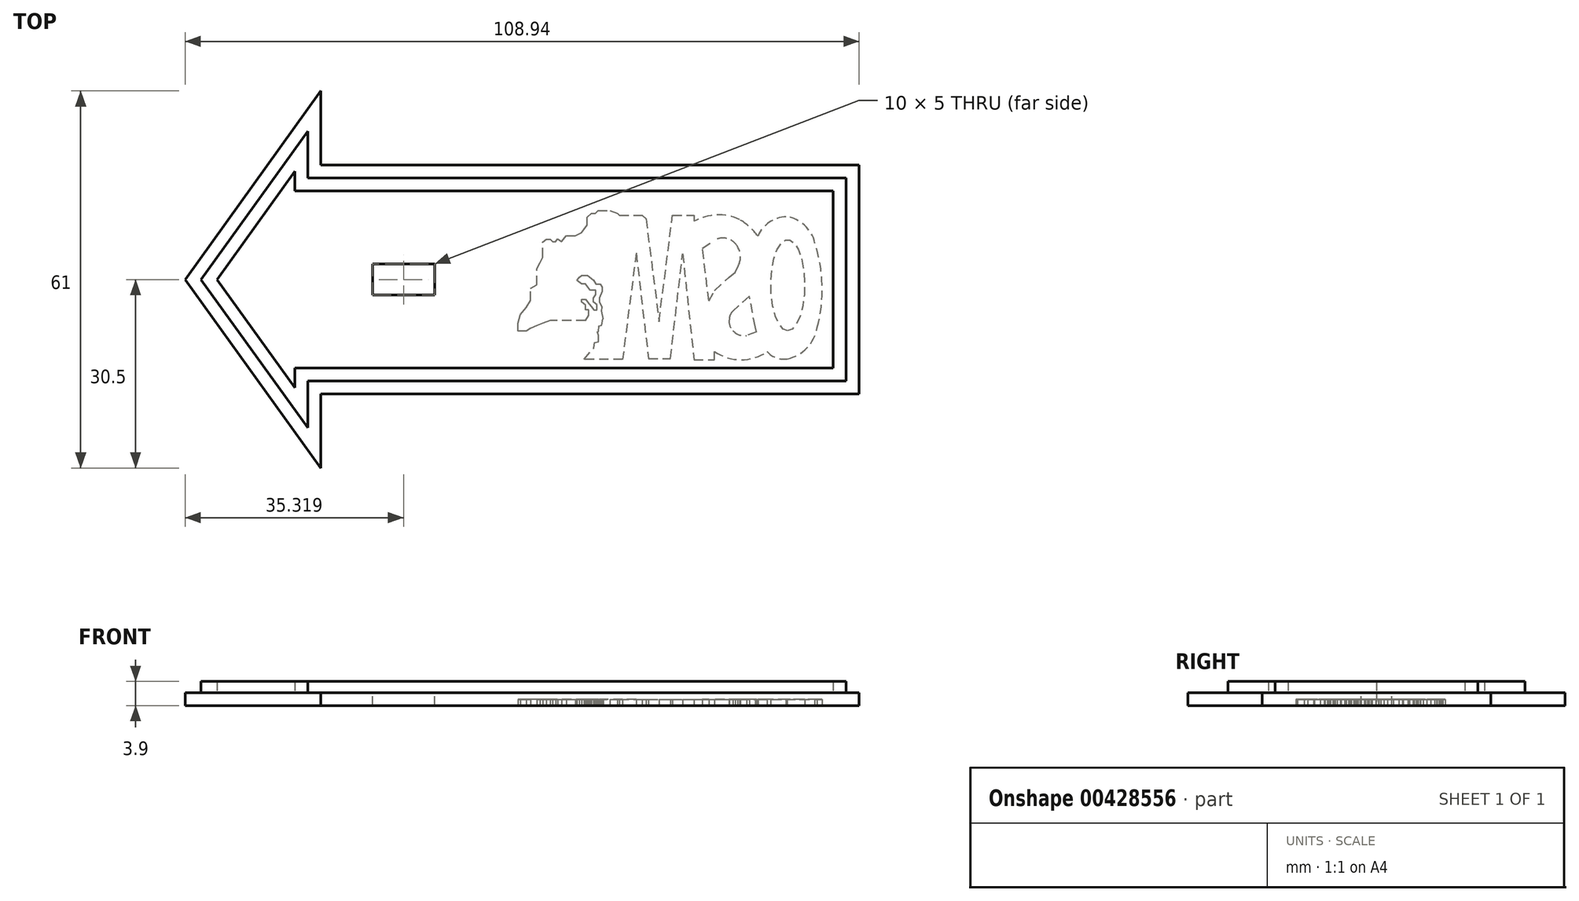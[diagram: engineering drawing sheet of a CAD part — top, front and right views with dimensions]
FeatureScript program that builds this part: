
annotation { "Feature Type Name" : "Feature", "Feature Type Description" : "" }
export const myFeature = defineFeature(function(context is Context, id is Id, definition is map)
    precondition{}
    {
        {
            var Q0;
            Q0=qCreatedBy(makeId("Top.planeOp"),FACE);
            var sketch = newSketch(context, id + "F0", { "sketchPlane" : qUnion([Q0])});
            skLineSegment(sketch, "E0.0", {"start": v(61.6, 18.5) * mm, "end": v(61.6, -18.5) * mm});
            skLineSegment(sketch, "E0.1", {"start": v(-25.4, 18.5) * mm, "end": v(61.6, 18.5) * mm});
            skLineSegment(sketch, "E0.3", {"start": v(-25.4, -18.5) * mm, "end": v(61.6, -18.5) * mm});
            skLineSegment(sketch, "E1", {"start": v(-25.4, 18.5) * mm, "end": v(-25.4, 30.5) * mm});
            skLineSegment(sketch, "E2", {"start": v(-25.4, 30.5) * mm, "end": v(-47.35, 0) * mm});
            skLineSegment(sketch, "E3", {"start": v(-47.35, 0) * mm, "end": v(-25.4, -30.5) * mm});
            skLineSegment(sketch, "E4", {"start": v(-25.4, -30.5) * mm, "end": v(-25.4, -18.5) * mm});
            skPoint(sketch, "E5", {"position": v(61.6, 0) * mm});
            skSolve(sketch);
        }
        {
            var Q0;
            Q0=makeQuery(id+"F0.imprint","IMPRINT",FACE,{"disambiguationData":[TD([[makeQuery(id+"F0.imprint","IMPRINT",EDGE,{"derivedFrom":sQuery(id+"F0.wireOp",EDGE,"E0.0")}),-1.0]])]});
            extrude(context, id + "F1", {"entities" : qUnion([Q0]), "depth" : 2.1 * mm});
        }
        {
            var Q0;
            Q0=makeQuery(id+"F1.opExtrude","CAP_FACE",FACE,{"disambiguationData":[OSD([sQuery(id+"F0.wireOp",EDGE,"E0.0"),sQuery(id+"F0.wireOp",EDGE,"E0.1"),sQuery(id+"F0.wireOp",EDGE,"E0.3"),sQuery(id+"F0.wireOp",EDGE,"E1"),sQuery(id+"F0.wireOp",EDGE,"E2"),sQuery(id+"F0.wireOp",EDGE,"E3"),sQuery(id+"F0.wireOp",EDGE,"E4")])],"isStart":false});
            var sketch = newSketch(context, id + "F2", { "sketchPlane" : qUnion([Q0])});
            skLineSegment(sketch, "E6.0", {"start": v(61.6, 18.5) * mm, "end": v(61.6, -18.5) * mm, "construction": true});
            skLineSegment(sketch, "E6.1", {"start": v(-25.4, 18.5) * mm, "end": v(61.6, 18.5) * mm, "construction": true});
            skLineSegment(sketch, "E6.3", {"start": v(-25.4, -18.5) * mm, "end": v(61.6, -18.5) * mm, "construction": true});
            skLineSegment(sketch, "E7", {"start": v(-25.4, 18.5) * mm, "end": v(-25.4, 30.5) * mm, "construction": true});
            skLineSegment(sketch, "E8", {"start": v(-25.4, 30.5) * mm, "end": v(-47.35, 0) * mm, "construction": true});
            skLineSegment(sketch, "E9", {"start": v(-47.35, 0) * mm, "end": v(-25.4, -30.5) * mm, "construction": true});
            skLineSegment(sketch, "E10", {"start": v(-25.4, -30.5) * mm, "end": v(-25.4, -18.5) * mm, "construction": true});
            skPoint(sketch, "E11", {"position": v(61.6, 0) * mm});
            skLineSegment(sketch, "E12.0", {"start": v(-27.5, 16.4) * mm, "end": v(-27.5, 23.99) * mm});
            skLineSegment(sketch, "E12.1", {"start": v(-27.5, 16.4) * mm, "end": v(59.5, 16.4) * mm});
            skLineSegment(sketch, "E12.2", {"start": v(-44.77, 0) * mm, "end": v(-27.5, -23.99) * mm});
            skLineSegment(sketch, "E12.3", {"start": v(-27.5, -23.99) * mm, "end": v(-27.5, -16.4) * mm});
            skLineSegment(sketch, "E12.4", {"start": v(-27.5, -16.4) * mm, "end": v(59.5, -16.4) * mm});
            skLineSegment(sketch, "E12.5", {"start": v(-27.5, 23.99) * mm, "end": v(-44.77, 0) * mm});
            skLineSegment(sketch, "E12.6", {"start": v(59.5, 16.4) * mm, "end": v(59.5, -16.4) * mm});
            skLineSegment(sketch, "E13.0", {"start": v(-29.6, 14.3) * mm, "end": v(-29.6, 17.47) * mm});
            skLineSegment(sketch, "E13.1", {"start": v(-29.6, 14.3) * mm, "end": v(57.4, 14.3) * mm});
            skLineSegment(sketch, "E13.2", {"start": v(-42.18, 0) * mm, "end": v(-29.6, -17.47) * mm});
            skLineSegment(sketch, "E13.3", {"start": v(-29.6, -17.47) * mm, "end": v(-29.6, -14.3) * mm});
            skLineSegment(sketch, "E13.4", {"start": v(-29.6, -14.3) * mm, "end": v(57.4, -14.3) * mm});
            skLineSegment(sketch, "E13.5", {"start": v(-29.6, 17.47) * mm, "end": v(-42.18, 0) * mm});
            skLineSegment(sketch, "E13.6", {"start": v(57.4, 14.3) * mm, "end": v(57.4, -14.3) * mm});
            skLineSegment(sketch, "E14", {"start": v(59.5, 0) * mm, "end": v(-15, 0) * mm, "construction": true});
            skPoint(sketch, "E14.endSnap0", {"position": v(59.5, 0) * mm});
            skSolve(sketch);
        }
        {
            var Q0;
            Q0=makeQuery(id+"F2.imprint","IMPRINT",FACE,{"disambiguationData":[TD([[makeQuery(id+"F2.imprint","IMPRINT",EDGE,{"derivedFrom":sQuery(id+"F2.wireOp",EDGE,"E12.0")}),1.0]])]});
            extrude(context, id + "F3", {"entities" : qUnion([Q0]), "operationType" : NewBodyOperationType.ADD, "depth" : 1.8 * mm, "offsetDistance" : 25 * mm});
        }
        {
            var Q0;
            Q0=makeQuery(id+"F3.boolean.opBoolean","SPLIT",FACE,{"disambiguationData":[TD([makeQuery(id+"F3.opExtrude","SWEPT_FACE",FACE,{"disambiguationData":[OSD([sQuery(id+"F2.wireOp",EDGE,"E13.0")])]})])],"derivedFrom":makeQuery(id+"F1.opExtrude","CAP_FACE",FACE,{"disambiguationData":[OSD([sQuery(id+"F0.wireOp",EDGE,"E0.0"),sQuery(id+"F0.wireOp",EDGE,"E0.1"),sQuery(id+"F0.wireOp",EDGE,"E0.3"),sQuery(id+"F0.wireOp",EDGE,"E1"),sQuery(id+"F0.wireOp",EDGE,"E2"),sQuery(id+"F0.wireOp",EDGE,"E3"),sQuery(id+"F0.wireOp",EDGE,"E4")])],"isStart":false})});
            var sketch = newSketch(context, id + "F4", { "sketchPlane" : qUnion([Q0])});
            skPoint(sketch, "E15", {"position": v(59.5, 0) * mm});
            skLineSegment(sketch, "E16", {"start": v(59.5, 0) * mm, "end": v(-7.03, 0) * mm, "construction": true});
            skLineSegment(sketch, "E17", {"start": v(-7.03, 0) * mm, "end": v(-7.03, -2.5) * mm});
            skLineSegment(sketch, "E18", {"start": v(-7.03, -2.5) * mm, "end": v(-17.03, -2.5) * mm});
            skLineSegment(sketch, "E19", {"start": v(-17.03, -2.5) * mm, "end": v(-17.03, 2.5) * mm});
            skLineSegment(sketch, "E20", {"start": v(-17.03, 2.5) * mm, "end": v(-7.03, 2.5) * mm});
            skLineSegment(sketch, "E21", {"start": v(-7.03, 2.5) * mm, "end": v(-7.03, 0) * mm});
            skSolve(sketch);
        }
        {
            var Q0;
            Q0=makeQuery(id+"F4.imprint","IMPRINT",FACE,{"disambiguationData":[TD([[makeQuery(id+"F4.imprint","IMPRINT",EDGE,{"derivedFrom":sQuery(id+"F4.wireOp",EDGE,"E17")}),-1.0]])]});
            extrude(context, id + "F5", {"entities" : qUnion([Q0]), "operationType" : NewBodyOperationType.REMOVE, "oppositeDirection" : true, "depth" : 8 * mm, "offsetDistance" : 25 * mm});
        }
        {
            var Q0;
            Q0=makeQuery(id+"F1.opExtrude","CAP_FACE",FACE,{"disambiguationData":[OSD([sQuery(id+"F0.wireOp",EDGE,"E0.0"),sQuery(id+"F0.wireOp",EDGE,"E0.1"),sQuery(id+"F0.wireOp",EDGE,"E0.3"),sQuery(id+"F0.wireOp",EDGE,"E1"),sQuery(id+"F0.wireOp",EDGE,"E2"),sQuery(id+"F0.wireOp",EDGE,"E3"),sQuery(id+"F0.wireOp",EDGE,"E4")])],"isStart":true});
            var sketch = newSketch(context, id + "F6", { "sketchPlane" : qUnion([Q0])});
            skLineSegment(sketch, "E22", {"start": v(17.39, 6.65) * mm, "end": v(15.72, 6.65) * mm});
            skLineSegment(sketch, "E23", {"start": v(15.72, 6.65) * mm, "end": v(11.67, 6.65) * mm});
            skLineSegment(sketch, "E24", {"start": v(11.67, 6.65) * mm, "end": v(10.46, 7.05) * mm});
            skLineSegment(sketch, "E25", {"start": v(10.46, 7.05) * mm, "end": v(9.5, 7.46) * mm});
            skLineSegment(sketch, "E26", {"start": v(9.5, 7.46) * mm, "end": v(8.48, 7.91) * mm});
            skLineSegment(sketch, "E27", {"start": v(8.48, 7.91) * mm, "end": v(7.78, 8.37) * mm});
            skLineSegment(sketch, "E28", {"start": v(7.78, 8.37) * mm, "end": v(6.46, 8.37) * mm});
            skLineSegment(sketch, "E29", {"start": v(6.46, 8.37) * mm, "end": v(6.46, 7.05) * mm});
            skLineSegment(sketch, "E30", {"start": v(6.46, 7.05) * mm, "end": v(6.87, 5.69) * mm});
            skLineSegment(sketch, "E31", {"start": v(6.87, 5.69) * mm, "end": v(7.83, 4.52) * mm});
            skLineSegment(sketch, "E32", {"start": v(7.83, 4.52) * mm, "end": v(8.48, 3.41) * mm});
            skLineSegment(sketch, "E33", {"start": v(8.48, 3.41) * mm, "end": v(8.48, 1.44) * mm});
            skLineSegment(sketch, "E34", {"start": v(8.48, 1.44) * mm, "end": v(9.5, 0.88) * mm});
            skLineSegment(sketch, "E35", {"start": v(9.5, 0.88) * mm, "end": v(9.5, -1.75) * mm});
            skLineSegment(sketch, "E36", {"start": v(9.5, -1.75) * mm, "end": v(10, -2.71) * mm});
            skLineSegment(sketch, "E37", {"start": v(10, -2.71) * mm, "end": v(10.46, -3.62) * mm});
            skLineSegment(sketch, "E38", {"start": v(10.46, -3.62) * mm, "end": v(10.46, -6.05) * mm});
            skLineSegment(sketch, "E39", {"start": v(10.46, -6.05) * mm, "end": v(11.01, -6.5) * mm});
            skLineSegment(sketch, "E40", {"start": v(11.01, -6.5) * mm, "end": v(11.67, -6.5) * mm});
            skLineSegment(sketch, "E41", {"start": v(11.67, -6.5) * mm, "end": v(12.08, -6.1) * mm});
            skLineSegment(sketch, "E42", {"start": v(12.08, -6.1) * mm, "end": v(12.53, -6.1) * mm});
            skLineSegment(sketch, "E43", {"start": v(12.53, -6.1) * mm, "end": v(12.9, -6.58) * mm});
            skLineSegment(sketch, "E44", {"start": v(12.9, -6.58) * mm, "end": v(13.53, -6.1) * mm});
            skLineSegment(sketch, "E45", {"start": v(13.53, -6.1) * mm, "end": v(14.3, -7.1) * mm});
            skLineSegment(sketch, "E46", {"start": v(14.3, -7.1) * mm, "end": v(15.72, -7.1) * mm});
            skLineSegment(sketch, "E47", {"start": v(15.72, -7.1) * mm, "end": v(16.74, -7.57) * mm});
            skLineSegment(sketch, "E48", {"start": v(16.74, -7.57) * mm, "end": v(17.14, -8.11) * mm});
            skLineSegment(sketch, "E49", {"start": v(17.14, -8.11) * mm, "end": v(17.64, -8.8) * mm});
            skLineSegment(sketch, "E50", {"start": v(17.64, -8.8) * mm, "end": v(17.64, -10.1) * mm});
            skLineSegment(sketch, "E51", {"start": v(17.64, -10.1) * mm, "end": v(18.36, -10.73) * mm});
            skLineSegment(sketch, "E52", {"start": v(18.36, -10.73) * mm, "end": v(18.94, -10.73) * mm});
            skLineSegment(sketch, "E53", {"start": v(18.94, -10.73) * mm, "end": v(19.4, -11.13) * mm});
            skLineSegment(sketch, "E54", {"start": v(19.4, -11.13) * mm, "end": v(21.33, -11.13) * mm});
            skLineSegment(sketch, "E55", {"start": v(21.33, -11.13) * mm, "end": v(22.5, -10.68) * mm});
            skLineSegment(sketch, "E56", {"start": v(22.5, -10.68) * mm, "end": v(22.86, -10.36) * mm});
            skLineSegment(sketch, "E57", {"start": v(22.86, -10.36) * mm, "end": v(26.55, -10.36) * mm});
            skLineSegment(sketch, "E58", {"start": v(26.55, -10.36) * mm, "end": v(27.16, -9.8) * mm});
            skLineSegment(sketch, "E59", {"start": v(27.16, -9.8) * mm, "end": v(29.25, 6.8) * mm});
            skLineSegment(sketch, "E60", {"start": v(29.25, 6.8) * mm, "end": v(31.43, -10.36) * mm});
            skLineSegment(sketch, "E61", {"start": v(31.43, -10.36) * mm, "end": v(34.92, -10.36) * mm});
            skLineSegment(sketch, "E62", {"start": v(34.92, -10.36) * mm, "end": v(34.92, -9.4) * mm});
            skArc(sketch, "E63", {"start": v(42.28, -9.71) * mm, "mid": v(43.89, -8.5) * mm, "end": v(45.26, -7.04) * mm});
            skArc(sketch, "E64", {"start": v(45.26, -7.04) * mm, "mid": v(47.07, -9.27) * mm, "end": v(49.8, -10.16) * mm});
            skArc(sketch, "E65", {"start": v(49.8, -10.16) * mm, "mid": v(52.78, -8.77) * mm, "end": v(54.43, -5.92) * mm});
            skArc(sketch, "E66", {"start": v(54.43, -5.92) * mm, "mid": v(55.61, 0.92) * mm, "end": v(54.8, 7.82) * mm});
            skArc(sketch, "E67", {"start": v(54.8, 7.82) * mm, "mid": v(53.16, 11.07) * mm, "end": v(49.98, 12.83) * mm});
            skArc(sketch, "E68", {"start": v(49.98, 12.83) * mm, "mid": v(48.2, 12.68) * mm, "end": v(46.75, 11.65) * mm});
            skArc(sketch, "E69", {"start": v(46.75, 11.65) * mm, "mid": v(42.5, 12.99) * mm, "end": v(38.24, 11.65) * mm});
            skLineSegment(sketch, "E70", {"start": v(25.56, -4.3) * mm, "end": v(27.54, 12.78) * mm});
            skLineSegment(sketch, "E71", {"start": v(27.54, 12.78) * mm, "end": v(31.1, 12.78) * mm});
            skLineSegment(sketch, "E72", {"start": v(31.1, 12.78) * mm, "end": v(33.08, -4.19) * mm});
            skLineSegment(sketch, "E73", {"start": v(33.08, -4.19) * mm, "end": v(34.9, 12.99) * mm});
            skPoint(sketch, "E73.endSnap0", {"position": v(42.5, 12.99) * mm});
            skLineSegment(sketch, "E74", {"start": v(34.9, 12.99) * mm, "end": v(38.24, 12.99) * mm});
            skLineSegment(sketch, "E75", {"start": v(38.24, 12.99) * mm, "end": v(38.24, 11.65) * mm});
            skEllipse(sketch, "E76", {"center": v(50.05, 0.92) * mm, "majorRadius": 7.36 * mm, "minorRadius": 2.73 * mm, "majorAxis": v(0, 1)});
            skPoint(sketch, "E76.centerSnap0", {"position": v(55.61, 0.92) * mm});
            skLineSegment(sketch, "E77", {"start": v(37.32, 3.49) * mm, "end": v(36.26, -5.08) * mm});
            skLineSegment(sketch, "E78", {"start": v(36.26, -5.08) * mm, "end": v(38.15, -6.3) * mm});
            skArc(sketch, "E79", {"start": v(38.15, -6.3) * mm, "mid": v(40.26, -6.63) * mm, "end": v(41.94, -5.3) * mm});
            skLineSegment(sketch, "E80", {"start": v(37.32, 3.49) * mm, "end": v(38.23, 1.82) * mm});
            skLineSegment(sketch, "E81", {"start": v(38.23, 1.82) * mm, "end": v(40.58, -0.38) * mm});
            skLineSegment(sketch, "E82", {"start": v(40.58, -0.38) * mm, "end": v(41.56, -1.2) * mm});
            skLineSegment(sketch, "E83", {"start": v(41.56, -1.2) * mm, "end": v(42.1, -2.27) * mm});
            skArc(sketch, "E84", {"start": v(41.94, -5.3) * mm, "mid": v(42.41, -3.81) * mm, "end": v(42.1, -2.27) * mm});
            skLineSegment(sketch, "E85", {"start": v(45, 8.47) * mm, "end": v(44.81, 7.64) * mm});
            skLineSegment(sketch, "E86", {"start": v(44.81, 7.64) * mm, "end": v(43.85, 2.69) * mm});
            skLineSegment(sketch, "E87", {"start": v(43.85, 2.69) * mm, "end": v(41.2, 5.1) * mm});
            skArc(sketch, "E88", {"start": v(40.62, 6.36) * mm, "mid": v(40.79, 5.67) * mm, "end": v(41.2, 5.1) * mm});
            skArc(sketch, "E89", {"start": v(41.2, 8.28) * mm, "mid": v(40.67, 7.4) * mm, "end": v(40.62, 6.36) * mm});
            skArc(sketch, "E90", {"start": v(43.43, 9.07) * mm, "mid": v(42.22, 8.96) * mm, "end": v(41.2, 8.28) * mm});
            skLineSegment(sketch, "E91", {"start": v(45, 8.47) * mm, "end": v(43.43, 9.07) * mm});
            skLineSegment(sketch, "E92", {"start": v(25.56, -4.3) * mm, "end": v(23.38, 12.9) * mm});
            skLineSegment(sketch, "E93", {"start": v(23.38, 12.9) * mm, "end": v(17.1, 12.9) * mm});
            skLineSegment(sketch, "E94", {"start": v(17.1, 12.9) * mm, "end": v(18.73, 11.1) * mm});
            skLineSegment(sketch, "E95", {"start": v(18.73, 11.1) * mm, "end": v(18.84, 10.2) * mm});
            skLineSegment(sketch, "E96", {"start": v(18.84, 10.2) * mm, "end": v(19.45, 10.05) * mm});
            skLineSegment(sketch, "E97", {"start": v(19.45, 10.05) * mm, "end": v(19.45, 9.07) * mm});
            skLineSegment(sketch, "E98", {"start": v(19.45, 9.07) * mm, "end": v(19.32, 8.47) * mm});
            skLineSegment(sketch, "E99", {"start": v(19.32, 8.47) * mm, "end": v(19.45, 8.43) * mm});
            skLineSegment(sketch, "E100", {"start": v(19.45, 8.43) * mm, "end": v(19.57, 7.5) * mm});
            skLineSegment(sketch, "E101", {"start": v(19.57, 7.5) * mm, "end": v(20.02, 7.4) * mm});
            skLineSegment(sketch, "E102", {"start": v(20.02, 7.4) * mm, "end": v(20.15, 6.36) * mm});
            skLineSegment(sketch, "E103", {"start": v(20.15, 6.36) * mm, "end": v(20.26, 6.33) * mm});
            skLineSegment(sketch, "E104", {"start": v(20.26, 6.33) * mm, "end": v(20, 5.12) * mm});
            skLineSegment(sketch, "E105", {"start": v(20, 5.12) * mm, "end": v(20.08, 4.45) * mm});
            skLineSegment(sketch, "E106", {"start": v(17.39, 6.65) * mm, "end": v(17.87, 5.8) * mm});
            skLineSegment(sketch, "E107", {"start": v(17.87, 5.8) * mm, "end": v(17.87, 4.9) * mm});
            skLineSegment(sketch, "E108", {"start": v(17.87, 4.9) * mm, "end": v(17.39, 4.9) * mm});
            skLineSegment(sketch, "E109", {"start": v(17.39, 4.9) * mm, "end": v(17.39, 4.14) * mm});
            skLineSegment(sketch, "E110", {"start": v(17.39, 4.14) * mm, "end": v(16.72, 3.66) * mm});
            skLineSegment(sketch, "E111", {"start": v(16.72, 3.66) * mm, "end": v(16.72, 3.18) * mm});
            skLineSegment(sketch, "E112", {"start": v(16.72, 3.18) * mm, "end": v(17.39, 3.18) * mm});
            skLineSegment(sketch, "E113", {"start": v(17.39, 3.18) * mm, "end": v(17.73, 3.66) * mm});
            skLineSegment(sketch, "E114", {"start": v(17.73, 3.66) * mm, "end": v(18.3, 4.38) * mm});
            skLineSegment(sketch, "E115", {"start": v(18.3, 4.38) * mm, "end": v(18.73, 4.95) * mm});
            skLineSegment(sketch, "E116", {"start": v(18.73, 4.95) * mm, "end": v(19.2, 4.95) * mm});
            skLineSegment(sketch, "E117", {"start": v(19.2, 4.95) * mm, "end": v(19.2, 4.09) * mm});
            skLineSegment(sketch, "E118", {"start": v(19.2, 4.09) * mm, "end": v(18.68, 3.66) * mm});
            skLineSegment(sketch, "E119", {"start": v(18.68, 3.66) * mm, "end": v(18.68, 3) * mm});
            skLineSegment(sketch, "E120", {"start": v(18.68, 3) * mm, "end": v(19.01, 2.46) * mm});
            skLineSegment(sketch, "E121", {"start": v(19.01, 2.46) * mm, "end": v(19.01, 1.75) * mm});
            skLineSegment(sketch, "E122", {"start": v(19.01, 1.75) * mm, "end": v(18.15, 1.75) * mm});
            skLineSegment(sketch, "E123", {"start": v(18.15, 1.75) * mm, "end": v(17.39, 0.75) * mm});
            skLineSegment(sketch, "E124", {"start": v(17.39, 0.75) * mm, "end": v(16.72, 0.75) * mm});
            skLineSegment(sketch, "E125", {"start": v(16.72, 0.75) * mm, "end": v(16, 0.12) * mm});
            skLineSegment(sketch, "E126", {"start": v(16, 0.12) * mm, "end": v(16.4, -0.33) * mm});
            skLineSegment(sketch, "E127", {"start": v(16.4, -0.33) * mm, "end": v(16.72, -0.69) * mm});
            skLineSegment(sketch, "E128", {"start": v(16.72, -0.69) * mm, "end": v(17.73, -0.69) * mm});
            skLineSegment(sketch, "E129", {"start": v(17.73, -0.69) * mm, "end": v(18.68, 0.08) * mm});
            skLineSegment(sketch, "E130", {"start": v(18.68, 0.08) * mm, "end": v(19.06, 0.7) * mm});
            skLineSegment(sketch, "E131", {"start": v(19.06, 0.7) * mm, "end": v(19.73, 0.7) * mm});
            skLineSegment(sketch, "E132", {"start": v(19.73, 0.7) * mm, "end": v(20.07, 1.22) * mm});
            skLineSegment(sketch, "E133", {"start": v(20.07, 1.22) * mm, "end": v(20.07, 1.94) * mm});
            skLineSegment(sketch, "E134", {"start": v(20.07, 1.94) * mm, "end": v(19.64, 3) * mm});
            skLineSegment(sketch, "E135", {"start": v(19.64, 3) * mm, "end": v(19.64, 3.66) * mm});
            skLineSegment(sketch, "E136", {"start": v(19.64, 3.66) * mm, "end": v(20.08, 4.45) * mm});
            skPoint(sketch, "E137.end.orphan", {"position": v(36.99, -10.36) * mm});
            skArc(sketch, "E138", {"start": v(34.92, -9.4) * mm, "mid": v(38.57, -10.43) * mm, "end": v(42.28, -9.71) * mm});
            skSolve(sketch);
        }
        {
            var Q0;
            Q0=makeQuery(id+"F6.imprint","IMPRINT",FACE,{"disambiguationData":[TD([[makeQuery(id+"F6.imprint","IMPRINT",EDGE,{"derivedFrom":sQuery(id+"F6.wireOp",EDGE,"E22")}),1.0]])]});
            extrude(context, id + "F7", {"entities" : qUnion([Q0]), "operationType" : NewBodyOperationType.REMOVE, "oppositeDirection" : true, "depth" : 1.02 * mm, "offsetDistance" : 25 * mm});
        }
    });
